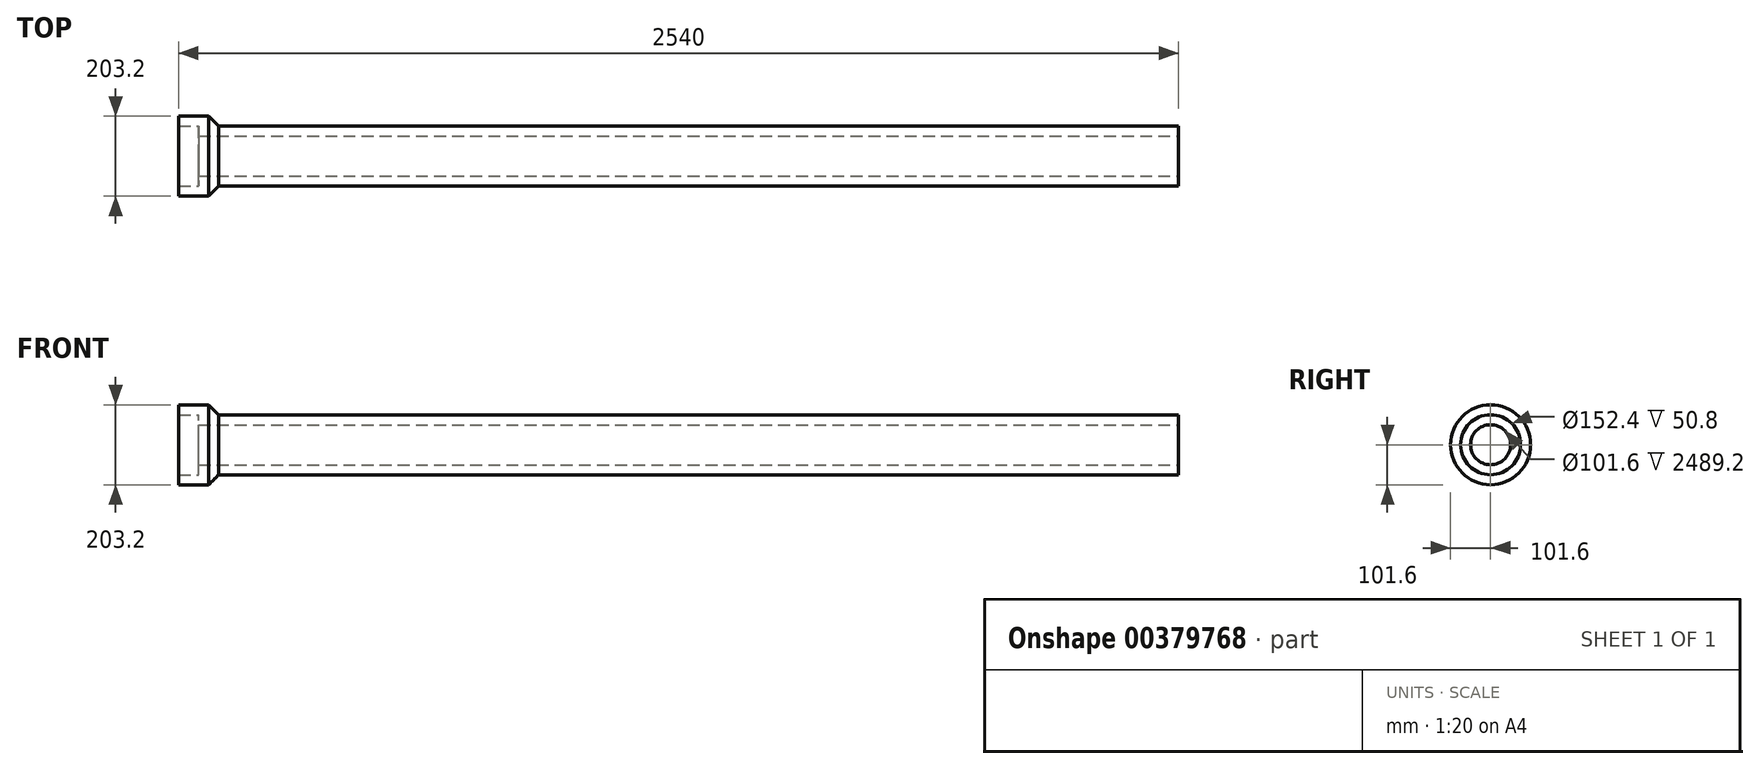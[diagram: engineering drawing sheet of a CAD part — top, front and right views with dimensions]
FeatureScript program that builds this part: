
annotation { "Feature Type Name" : "Feature", "Feature Type Description" : "" }
export const myFeature = defineFeature(function(context is Context, id is Id, definition is map)
    precondition{}
    {
        {
            var Q0;
            Q0=qCreatedBy(makeId("Front.planeOp"),FACE);
            var sketch = newSketch(context, id + "F0", { "sketchPlane" : qUnion([Q0])});
            skLineSegment(sketch, "E0.right", {"start": v(1270, 50.8) * mm, "end": v(1270, 76.2) * mm});
            skLineSegment(sketch, "E1.top", {"start": v(-1270, 101.6) * mm, "end": v(-1168.4, 101.6) * mm});
            skLineSegment(sketch, "E1.left", {"start": v(-1270, 76.2) * mm, "end": v(-1270, 101.6) * mm});
            skLineSegment(sketch, "E1.right", {"start": v(-1168.4, 76.2) * mm, "end": v(-1168.4, 101.6) * mm});
            skLineSegment(sketch, "E2.top", {"start": v(-1270, 101.6) * mm, "end": v(-1219.2, 101.6) * mm});
            skLineSegment(sketch, "E3.top", {"start": v(-1219.2, 50.8) * mm, "end": v(1270, 50.8) * mm});
            skLineSegment(sketch, "E3.right", {"start": v(1270, 76.2) * mm, "end": v(1270, 50.8) * mm});
            skLineSegment(sketch, "E4", {"start": v(-1168.4, 76.2) * mm, "end": v(1270, 76.2) * mm});
            skLineSegment(sketch, "E5", {"start": v(1270, 0) * mm, "end": v(-1270, 0) * mm});
            skLineSegment(sketch, "E6", {"start": v(-1270, 76.2) * mm, "end": v(-1219.2, 76.2) * mm});
            skLineSegment(sketch, "E7", {"start": v(-1219.2, 76.2) * mm, "end": v(-1219.2, 50.8) * mm});
            skSolve(sketch);
        }
        {
            var Q0;
            Q0=makeQuery(id+"F0.imprint","IMPRINT",FACE,{"disambiguationData":[TD([[makeQuery(id+"F0.imprint","IMPRINT",EDGE,{"derivedFrom":sQuery(id+"F0.wireOp",EDGE,"E1.top")}),-1.0]])]});
            var Q1;
            Q1=sQuery(id+"F0.wireOp",EDGE,"E5");
            revolve(context, id + "F1", {"entities" : qUnion([Q0]), "axis" : qUnion([Q1]), "revolveType" : RevolveType.FULL});
        }
        {
            var Q0;
            Q0=makeQuery(id+"F1.opRevolve","SWEPT_EDGE",EDGE,{"disambiguationData":[OSD([sQuery(id+"F0.wireOp",EDGE,"E1.top"),sQuery(id+"F0.wireOp",EDGE,"E1.right")])]});
            chamfer(context, id + "F2", {"entities" : qUnion([Q0]), "width" : 25.4 * mm, "tangentPropagation" : true});
        }
    });
